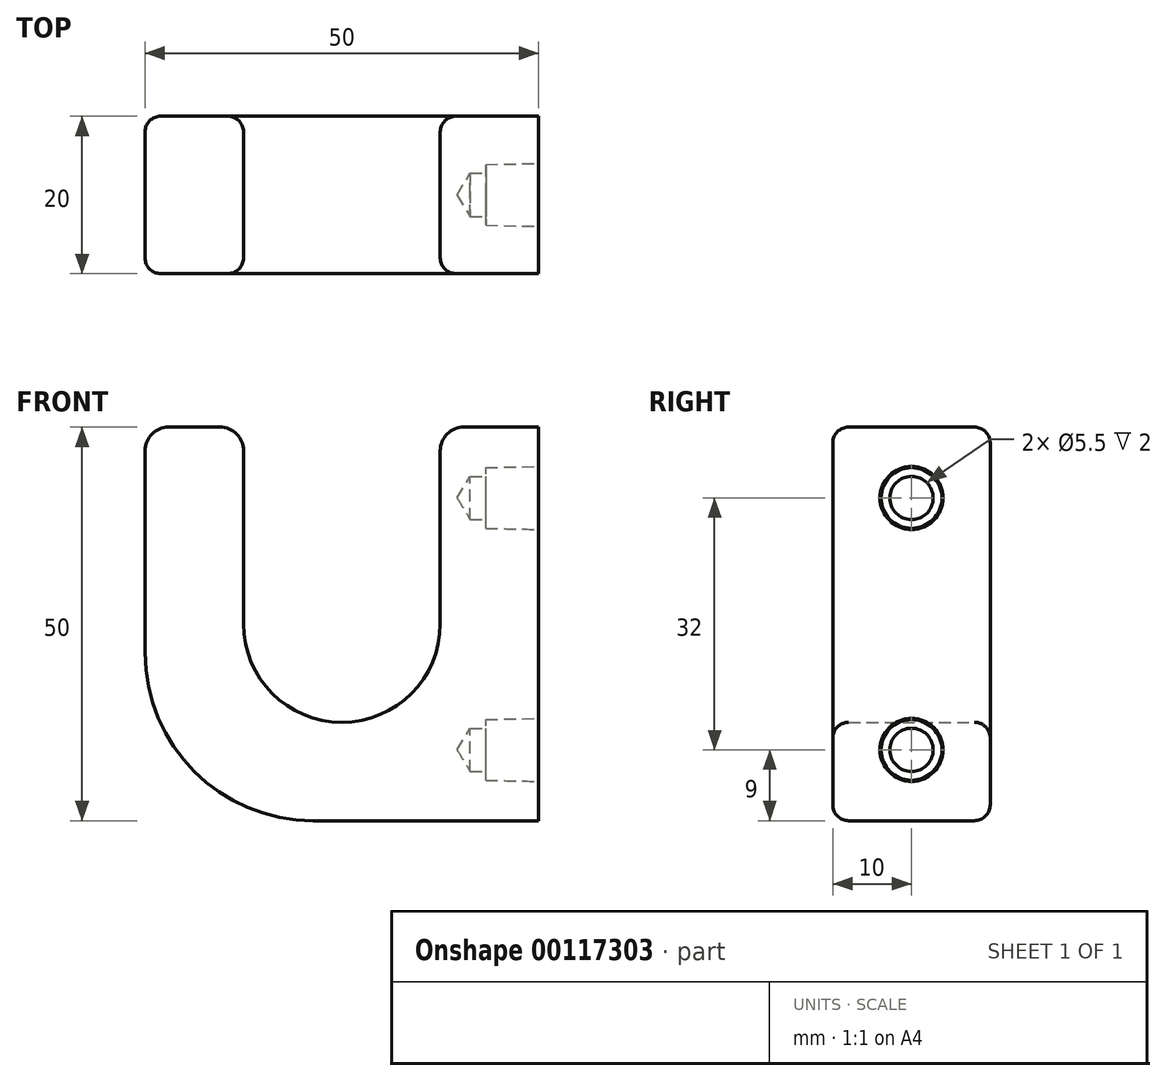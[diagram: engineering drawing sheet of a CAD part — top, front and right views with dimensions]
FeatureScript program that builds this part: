
annotation { "Feature Type Name" : "Feature", "Feature Type Description" : "" }
export const myFeature = defineFeature(function(context is Context, id is Id, definition is map)
    precondition{}
    {
        {
            var Q0;
            Q0=qCreatedBy(makeId("Front.planeOp"),FACE);
            var sketch = newSketch(context, id + "F0", { "sketchPlane" : qUnion([Q0])});
            skLineSegment(sketch, "E0.bottom", {"start": v(25, -25) * mm, "end": v(-25, -25) * mm});
            skLineSegment(sketch, "E0.top", {"start": v(25, 25) * mm, "end": v(-25, 25) * mm});
            skLineSegment(sketch, "E0.left", {"start": v(25, -25) * mm, "end": v(25, 25) * mm});
            skLineSegment(sketch, "E0.right", {"start": v(-25, -25) * mm, "end": v(-25, 25) * mm});
            skArc(sketch, "E1", {"start": v(-12.5, 0) * mm, "mid": v(0, -12.5) * mm, "end": v(12.5, 0) * mm});
            skLineSegment(sketch, "E2", {"start": v(-12.5, 0) * mm, "end": v(-12.5, 25) * mm});
            skLineSegment(sketch, "E3", {"start": v(-12.5, 25) * mm, "end": v(12.5, 25) * mm});
            skLineSegment(sketch, "E4", {"start": v(12.5, 25) * mm, "end": v(12.5, 0) * mm});
            skSolve(sketch);
        }
        {
            var Q0;
            Q0=makeQuery(id+"F0.imprint","IMPRINT",FACE,{"disambiguationData":[TD([[makeQuery(id+"F0.imprint","IMPRINT",EDGE,{"derivedFrom":sQuery(id+"F0.wireOp",EDGE,"E0.bottom")}),-1.0]])]});
            extrude(context, id + "F1", {"entities" : qUnion([Q0]), "depth" : 20 * mm});
        }
        {
            var Q0;
            Q0=makeQuery(id+"F1.opExtrude","SWEPT_EDGE",EDGE,{"disambiguationData":[OSD([sQuery(id+"F0.wireOp",EDGE,"E0.top"),sQuery(id+"F0.wireOp",EDGE,"E3"),sQuery(id+"F0.wireOp",EDGE,"E4")])]});
            var Q1;
            Q1=makeQuery(id+"F1.opExtrude","SWEPT_EDGE",EDGE,{"disambiguationData":[OSD([sQuery(id+"F0.wireOp",EDGE,"E0.top"),sQuery(id+"F0.wireOp",EDGE,"E2"),sQuery(id+"F0.wireOp",EDGE,"E3")])]});
            var Q2;
            Q2=makeQuery(id+"F1.opExtrude","SWEPT_EDGE",EDGE,{"disambiguationData":[OSD([sQuery(id+"F0.wireOp",EDGE,"E0.top"),sQuery(id+"F0.wireOp",EDGE,"E0.right")])]});
            fillet(context, id + "F2", {"entities" : qUnion([Q0, Q1, Q2]), "radius" : 3 * mm, "tangentPropagation" : true, "allowEdgeOverflow" : false});
        }
        {
            var Q0;
            Q0=makeQuery(id+"F1.opExtrude","SWEPT_EDGE",EDGE,{"disambiguationData":[OSD([sQuery(id+"F0.wireOp",EDGE,"E0.bottom"),sQuery(id+"F0.wireOp",EDGE,"E0.right")])]});
            fillet(context, id + "F3", {"entities" : qUnion([Q0]), "radius" : 21.37 * mm, "tangentPropagation" : true, "allowEdgeOverflow" : false});
        }
        {
            var Q0;
            Q0=makeQuery(id+"F1.opExtrude","SWEPT_FACE",FACE,{"disambiguationData":[OSD([sQuery(id+"F0.wireOp",EDGE,"E0.left")])]});
            var sketch = newSketch(context, id + "F4", { "sketchPlane" : qUnion([Q0])});
            skPoint(sketch, "E5", {"position": v(-20, 16) * mm});
            skPoint(sketch, "E6", {"position": v(-20, -16) * mm});
            skPoint(sketch, "E7", {"position": v(-10, 25) * mm});
            skPoint(sketch, "E8", {"position": v(0, 25) * mm});
            skPoint(sketch, "E9", {"position": v(-10, -25) * mm});
            skLineSegment(sketch, "E10", {"start": v(-20, 16) * mm, "end": v(0, 16) * mm, "construction": true});
            skLineSegment(sketch, "E11", {"start": v(-20, -16) * mm, "end": v(0, -16) * mm, "construction": true});
            skPoint(sketch, "E12", {"position": v(-10, 16) * mm});
            skPoint(sketch, "E13", {"position": v(-10, -16) * mm});
            skCircle(sketch, "E14", {"center": v(-10, 16) * mm, "radius": 4 * mm});
            skCircle(sketch, "E15", {"center": v(-10, -16) * mm, "radius": 4 * mm});
            skSolve(sketch);
        }
        {
            var Q0;
            Q0=makeQuery(id+"F4.imprint","IMPRINT",FACE,{"disambiguationData":[TD([[makeQuery(id+"F4.imprint","IMPRINT",EDGE,{"derivedFrom":sQuery(id+"F4.wireOp",EDGE,"E14")}),-1.0]])]});
            cPlane(context, id + "F5", {"entities" : qUnion([Q0]), "cplaneType" : CPlaneType.OFFSET, "offset" : 6.7 * mm, "oppositeDirection" : true, "width" : 150 * mm, "height" : 150 * mm});
        }
        {
            var Q0;
            Q0=qCreatedBy(id+"F5.planeOp",FACE);
            var sketch = newSketch(context, id + "F6", { "sketchPlane" : qUnion([Q0])});
            skPoint(sketch, "E16", {"position": v(-10, 16) * mm});
            skPoint(sketch, "E17", {"position": v(-10, -16) * mm});
            skCircle(sketch, "E18", {"center": v(-10, 16) * mm, "radius": 3.85 * mm});
            skCircle(sketch, "E19", {"center": v(-10, -16) * mm, "radius": 3.85 * mm});
            skSolve(sketch);
        }
        {
            var Q0;
            Q0=makeQuery(id+"F4.imprint","IMPRINT",FACE,{"disambiguationData":[TD([[makeQuery(id+"F4.imprint","IMPRINT",EDGE,{"derivedFrom":sQuery(id+"F4.wireOp",EDGE,"E14")}),1.0]])]});
            var Q1;
            Q1=makeQuery(id+"F4.imprint","IMPRINT",FACE,{"disambiguationData":[TD([[makeQuery(id+"F4.imprint","IMPRINT",EDGE,{"derivedFrom":sQuery(id+"F4.wireOp",EDGE,"E15")}),1.0]])]});
            var Q2;
            Q2=sQuery(id+"F4.wireOp",EDGE,"E14");
            var Q3;
            Q3=sQuery(id+"F6.wireOp",EDGE,"E18");
            extrude(context, id + "F7", {"entities" : qUnion([Q0, Q1]), "operationType" : NewBodyOperationType.REMOVE, "surfaceEntities" : qUnion([Q2, Q3]), "oppositeDirection" : true, "depth" : 6.7 * mm, "hasDraft" : true, "draftAngle" : 1.25 * degree, "draftPullDirection" : true});
        }
        {
            var Q0;
            Q0=sQuery(id+"F4.wireOp",VERTEX,"E12");
            var Q1;
            Q1=sQuery(id+"F4.wireOp",VERTEX,"E13");
            var Q2;
            Q2=makeQuery(id+"F1.opExtrude","SWEPT_BODY",BODY,{"disambiguationData":[OSD([sQuery(id+"F0.wireOp",EDGE,"E0.bottom"),sQuery(id+"F0.wireOp",EDGE,"E0.top"),sQuery(id+"F0.wireOp",EDGE,"E0.left"),sQuery(id+"F0.wireOp",EDGE,"E0.right"),sQuery(id+"F0.wireOp",EDGE,"E1"),sQuery(id+"F0.wireOp",EDGE,"E2"),sQuery(id+"F0.wireOp",EDGE,"E4")])]});
            hole(context, id + "F8", {"style" : HoleStyle.SIMPLE, "endStyle" : HoleEndStyle.BLIND, "standardTappedOrClearance" : lookupTablePath({ "standard" : "ISO", "fit" : "Normal", "size" : "M5", "type" : "Clearance" }), "standardBlindInLast" : lookupTablePath({ "fit" : "Standard", "standard" : "ISO", "size" : "M5", "type" : "Clearance" }), "holeDiameter" : 5.5 * mm, "holeDepth" : 2 * mm, "locations" : qUnion([Q0, Q1]), "scope" : qUnion([Q2])});
        }
        {
            var Q0;
            {var subQ0=sQuery(id+"F0.wireOp",EDGE,"E0.top");Q0=makeQuery(id+"F1.opExtrude","CAP_EDGE",EDGE,{"disambiguationData":[OSD([subQ0]),TDD([makeQuery(id+"F0.imprint","IMPRINT",EDGE,{"disambiguationData":[TD([[makeQuery(id+"F0.imprint","INTERSECT",VERTEX,{"derivedFrom":[subQ0,sQuery(id+"F0.wireOp",EDGE,"E0.left")]}),-1.0]])],"derivedFrom":subQ0})])],"isStart":true});}
            var Q1;
            {var subQ0=sQuery(id+"F0.wireOp",EDGE,"E0.top");Q1=makeQuery(id+"F1.opExtrude","CAP_EDGE",EDGE,{"disambiguationData":[OSD([subQ0]),TDD([makeQuery(id+"F0.imprint","IMPRINT",EDGE,{"disambiguationData":[TD([[makeQuery(id+"F0.imprint","INTERSECT",VERTEX,{"derivedFrom":[subQ0,sQuery(id+"F0.wireOp",EDGE,"E0.left")]}),-1.0]])],"derivedFrom":subQ0})])],"isStart":false});}
            fillet(context, id + "F9", {"entities" : qUnion([Q0, Q1]), "radius" : 2 * mm, "tangentPropagation" : true, "allowEdgeOverflow" : false});
        }
    });
